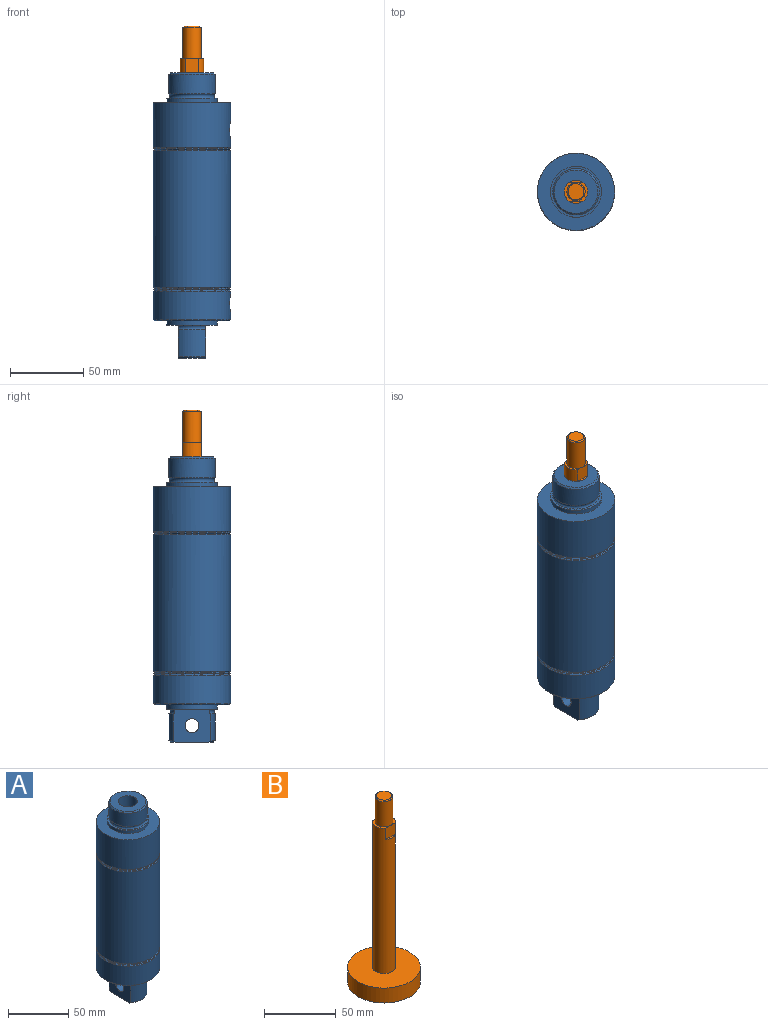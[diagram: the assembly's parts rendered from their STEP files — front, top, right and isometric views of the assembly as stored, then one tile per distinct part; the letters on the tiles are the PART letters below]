
ASSEMBLY  parts=2 mates=1
PART A: 43 faces, bbox 53.1x53.1x195.3 mm
  f0: torus R=17.02mm, axis (0,0,1), area 72mm2, adj f27,f35,f37,f38
  f1: torus R=17.02mm, axis (0,0,1), area 341.3mm2, adj f21,f31
  f2: torus R=17.02mm, axis (0,0,1), area 72mm2, adj f34,f35,f37,f38
  f3: cylinder r=5.56mm len=11.13mm, axis (1,0,0), area 333.7mm2, adj f25,f42
  f4: cone r=6.24mm half-angle=1.7deg, axis (1,0,0), area 369.3mm2, adj f23,f42
  f5: cylinder r=5.56mm len=15.38mm, axis (1,0,0), area 537.5mm2, adj f6,f41
  f6: cone r=5.56mm half-angle=59deg, axis (1,0,0), area 113.4mm2, adj f5
  f7: cone r=6.24mm half-angle=1.7deg, axis (1,0,0), area 369.3mm2, adj f11,f41
  f8: cylinder r=4.76mm len=19.05mm, axis (1,0,0), area 570mm2, adj f37,f38
  f9: cone r=26.42mm half-angle=45deg, axis (0,0,1), area 176.3mm2, adj f11,f36
  f10: cone r=14.86mm half-angle=45deg, axis (0,0,-1), area 138.7mm2, adj f21,f30
  f11: cylinder r=26.42mm len=52.83mm, axis (0,0,-1), area 3123.1mm2, adj f7,f9,f13
  f12: cylinder r=17.44mm len=34.89mm, axis (0,0,1), area 334.1mm2, adj f35,f36
  f13: cone r=25.74mm half-angle=45deg, axis (0,0,-1), area 156mm2, adj f11,f14
  f14: cone r=26.34mm half-angle=45deg, axis (0,0,1), area 138.1mm2, adj f13,f15
  f15: cone r=25.74mm half-angle=45deg, axis (0,0,-1), area 138.1mm2, adj f14,f16
  f16: cone r=26.42mm half-angle=45deg, axis (0,0,1), area 156mm2, adj f15,f24
  f17: cone r=25.74mm half-angle=45deg, axis (0,0,-1), area 156mm2, adj f18,f24
  f18: cone r=26.34mm half-angle=45deg, axis (0,0,1), area 138.1mm2, adj f17,f19
  f19: cone r=25.74mm half-angle=45deg, axis (0,0,-1), area 138.1mm2, adj f18,f20
  f20: cone r=26.42mm half-angle=45deg, axis (0,0,1), area 156mm2, adj f19,f23
  f21: cylinder r=15.88mm len=31.75mm, axis (0,0,1), area 1342.8mm2, adj f1,f10
  f22: cylinder r=17.44mm len=34.89mm, axis (0,0,-1), area 334.1mm2, adj f31,f32
  f23: cylinder r=26.42mm len=52.83mm, axis (0,0,-1), area 4894mm2, adj f4,f20,f32
  f24: cylinder r=26.42mm len=93.47mm, axis (0,0,-1), area 15514.2mm2, adj f16,f17
  f25: cylinder r=7.94mm len=63.37mm, axis (0,0,-1), area 3055.7mm2, adj f3,f28,f30
  f26: cylinder r=25.4mm len=63.5mm, axis (0,0,-1), area 10134.1mm2, adj f28,f29
  f27: cylinder r=15.88mm len=19.05mm, axis (0,0,1), area 373.6mm2, adj f0,f37,f38,f39
  f28: plane 50.8x50.8mm, normal (0,0,-1), area 1828.9mm2, adj f25,f26
  f29: plane 50.8x50.8mm, normal (0,0,1), area 2026.8mm2, adj f26
  f30: plane 29.72x29.72mm, normal (0,0,1), area 495.7mm2, adj f10,f25
  f31: plane 34.89x34.89mm, normal (0,0,1), area 164.2mm2, adj f1,f22
  f32: plane 52.83x52.83mm, normal (0,0,1), area 1236.3mm2, adj f22,f23
  f33: plane 29.72x19.05mm, normal (0,0,-1), area 524.5mm2, adj f37,f38,f39,f40
  f34: cylinder r=15.88mm len=19.05mm, axis (0,0,1), area 373.6mm2, adj f2,f37,f38,f40
  f35: plane 34.89x34.89mm, normal (0,0,-1), area 389.6mm2, adj f0,f2,f12,f37,f38
  f36: plane 51.31x51.31mm, normal (0,0,-1), area 1111.7mm2, adj f9,f12
  f37: plane 25.65x22.6mm, normal (1,0,0), area 491.1mm2, adj f0,f2,f8,f27,f33,f34,f35,f39
  f38: plane 25.65x22.6mm, normal (-1,0,0), area 491.1mm2, adj f0,f2,f8,f27,f33,f34,f35,f39
  f39: cone r=15.88mm half-angle=45deg, axis (0,0,1), area 29.6mm2, adj f27,f33,f37,f38
  f40: cone r=15.88mm half-angle=45deg, axis (0,0,1), area 29.6mm2, adj f33,f34,f37,f38
  f41: plane 11.89x11.89mm, normal (1,0,0), area 13.8mm2, adj f5,f7
  f42: plane 11.89x11.89mm, normal (1,0,0), area 13.8mm2, adj f3,f4
PART B: 12 faces, bbox 50.8x50.8x158.9 mm
  f0: cone r=5.47mm half-angle=45deg, axis (0,0,-1), area 39.6mm2, adj f3,f7
  f1: cylinder r=25.4mm len=50.8mm, axis (0,0,-1), area 2026.8mm2, adj f4,f5
  f2: cylinder r=7.94mm len=123.83mm, axis (0,0,-1), area 5978.3mm2, adj f4,f6,f8,f9,f10,f11
  f3: cylinder r=6.23mm len=21.59mm, axis (0,0,-1), area 845.2mm2, adj f0,f6
  f4: plane 50.8x50.8mm, normal (0,0,1), area 1828.9mm2, adj f1,f2
  f5: plane 50.8x50.8mm, normal (0,0,-1), area 2026.8mm2, adj f1
  f6: plane 15.88x12.7mm, normal (0,0,1), area 55.4mm2, adj f2,f3,f8,f10
  f7: plane 10.94x10.94mm, normal (0,0,1), area 94mm2, adj f0
  f8: plane 9.65x9.53mm, normal (0,1,0), area 91.9mm2, adj f2,f6,f9
  f9: plane 9.53x1.59mm, normal (0,0,1), area 10.3mm2, adj f2,f8
  f10: plane 9.65x9.53mm, normal (0,-1,0), area 91.9mm2, adj f2,f6,f11
  f11: plane 9.53x1.59mm, normal (0,0,1), area 10.3mm2, adj f2,f10
PLACE A t=(0,0,-53.59)mm
PLACE B t=(0,0,59.65)mm
MATE slider B.f0 <-> A.f0  axis (0,0,1) through (0,0,-9.65)mm
